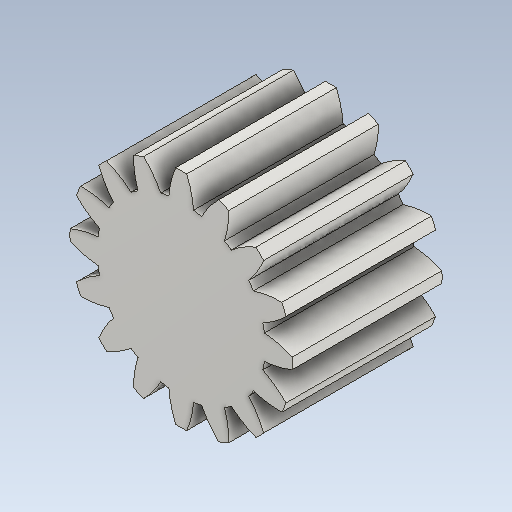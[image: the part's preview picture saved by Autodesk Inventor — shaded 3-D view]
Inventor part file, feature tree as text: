
AUTODESK INVENTOR PART (.ipt)
format: ipt  version: 2020.3 (Build 243373000, 373)  size: 246,784 bytes
history: native  units: mm (DEFAULTED — no unit token found)
features: plane x3, other x3, sketch x2, extrude x1
ambient origin geometry x8: Origin, YZ Plane, XZ Plane, XY Plane, X Axis, Y Axis, Z Axis, Center Point
bodies: Solid1 (feature_tree)
feature tree (9):
  extrude  "Extrusion1"  Depth=48.0mm TaperAngle=0.0deg
  plane  "Work Plane2"
  plane  "Work Plane8"
  plane  "Work Plane9"
  other  "Spur Gear"
  sketch  "Sketch1"  dims[d0=71.400418mm d1=48.0mm d2=0.0mm]
  sketch  "Sketch2"  dims[d3=65.361702mm d4=10.0mm d5=0.0mm d16=192.0mm d17=0.0mm d34=1.963495mm d39=0.0mm d41=0.0mm d43=192.0mm d46=192.0mm d47=0.0mm d48=0.0mm]
  other  "Srf1"
  other  "Pitch Diameter"
